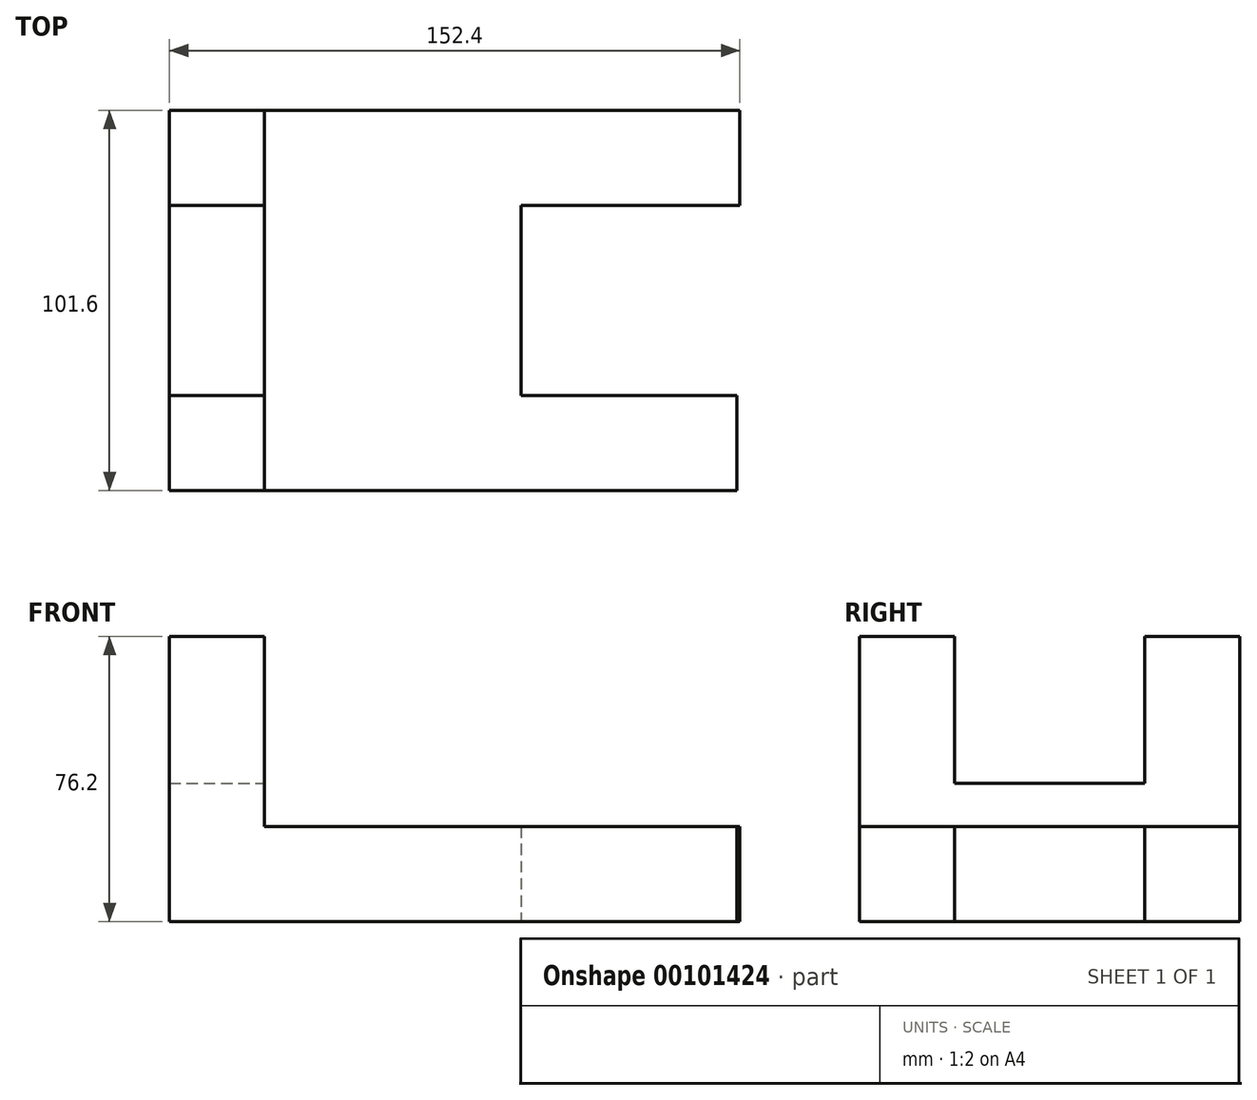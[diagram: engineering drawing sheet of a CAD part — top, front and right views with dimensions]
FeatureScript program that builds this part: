
annotation { "Feature Type Name" : "Feature", "Feature Type Description" : "" }
export const myFeature = defineFeature(function(context is Context, id is Id, definition is map)
    precondition{}
    {
        {
            var Q0;
            Q0=qCreatedBy(makeId("Top.planeOp"),FACE);
            var sketch = newSketch(context, id + "F0", { "sketchPlane" : qUnion([Q0])});
            skLineSegment(sketch, "E0", {"start": v(-114.53, 22.92) * mm, "end": v(-114.53, -78.68) * mm});
            skLineSegment(sketch, "E1", {"start": v(-114.53, -78.68) * mm, "end": v(11.62, -78.68) * mm});
            skLineSegment(sketch, "E2", {"start": v(11.62, -78.68) * mm, "end": v(11.62, -53.28) * mm});
            skLineSegment(sketch, "E3", {"start": v(11.62, -53.28) * mm, "end": v(-46, -53.28) * mm});
            skLineSegment(sketch, "E4", {"start": v(-46, -53.28) * mm, "end": v(-46, -2.48) * mm});
            skLineSegment(sketch, "E5", {"start": v(-46, -2.48) * mm, "end": v(12.47, -2.48) * mm});
            skLineSegment(sketch, "E6", {"start": v(12.47, -2.48) * mm, "end": v(12.47, 22.92) * mm});
            skLineSegment(sketch, "E7", {"start": v(12.47, 22.92) * mm, "end": v(-114.53, 22.92) * mm});
            skSolve(sketch);
        }
        {
            var Q0;
            Q0=makeQuery(id+"F0.imprint","IMPRINT",FACE,{"disambiguationData":[TD([[makeQuery(id+"F0.imprint","IMPRINT",EDGE,{"derivedFrom":sQuery(id+"F0.wireOp",EDGE,"E0")}),1.0]])]});
            extrude(context, id + "F1", {"entities" : qUnion([Q0]), "depth" : 25.4 * mm});
        }
        {
            var Q0;
            Q0=makeQuery(id+"F1.opExtrude","SWEPT_FACE",FACE,{"disambiguationData":[OSD([sQuery(id+"F0.wireOp",EDGE,"E0")])]});
            var sketch = newSketch(context, id + "F2", { "sketchPlane" : qUnion([Q0])});
            skLineSegment(sketch, "E8", {"start": v(-22.92, 0) * mm, "end": v(-22.92, 76.2) * mm});
            skLineSegment(sketch, "E9", {"start": v(-22.92, 76.2) * mm, "end": v(2.48, 76.2) * mm});
            skLineSegment(sketch, "E10", {"start": v(2.48, 76.2) * mm, "end": v(2.48, 36.93) * mm});
            skLineSegment(sketch, "E11", {"start": v(2.48, 36.93) * mm, "end": v(53.28, 36.93) * mm});
            skLineSegment(sketch, "E12", {"start": v(53.28, 36.93) * mm, "end": v(53.28, 76.17) * mm});
            skLineSegment(sketch, "E13", {"start": v(53.28, 76.17) * mm, "end": v(78.68, 76.17) * mm});
            skLineSegment(sketch, "E14", {"start": v(78.68, 76.17) * mm, "end": v(78.68, 0) * mm});
            skLineSegment(sketch, "E15", {"start": v(78.68, 0) * mm, "end": v(-22.92, 0) * mm});
            skSolve(sketch);
        }
        {
            var Q0;
            Q0 = qSketchRegion(id + "F2", true);
            extrude(context, id + "F3", {"entities" : qUnion([Q0]), "operationType" : NewBodyOperationType.ADD, "depth" : 25.4 * mm});
        }
    });
